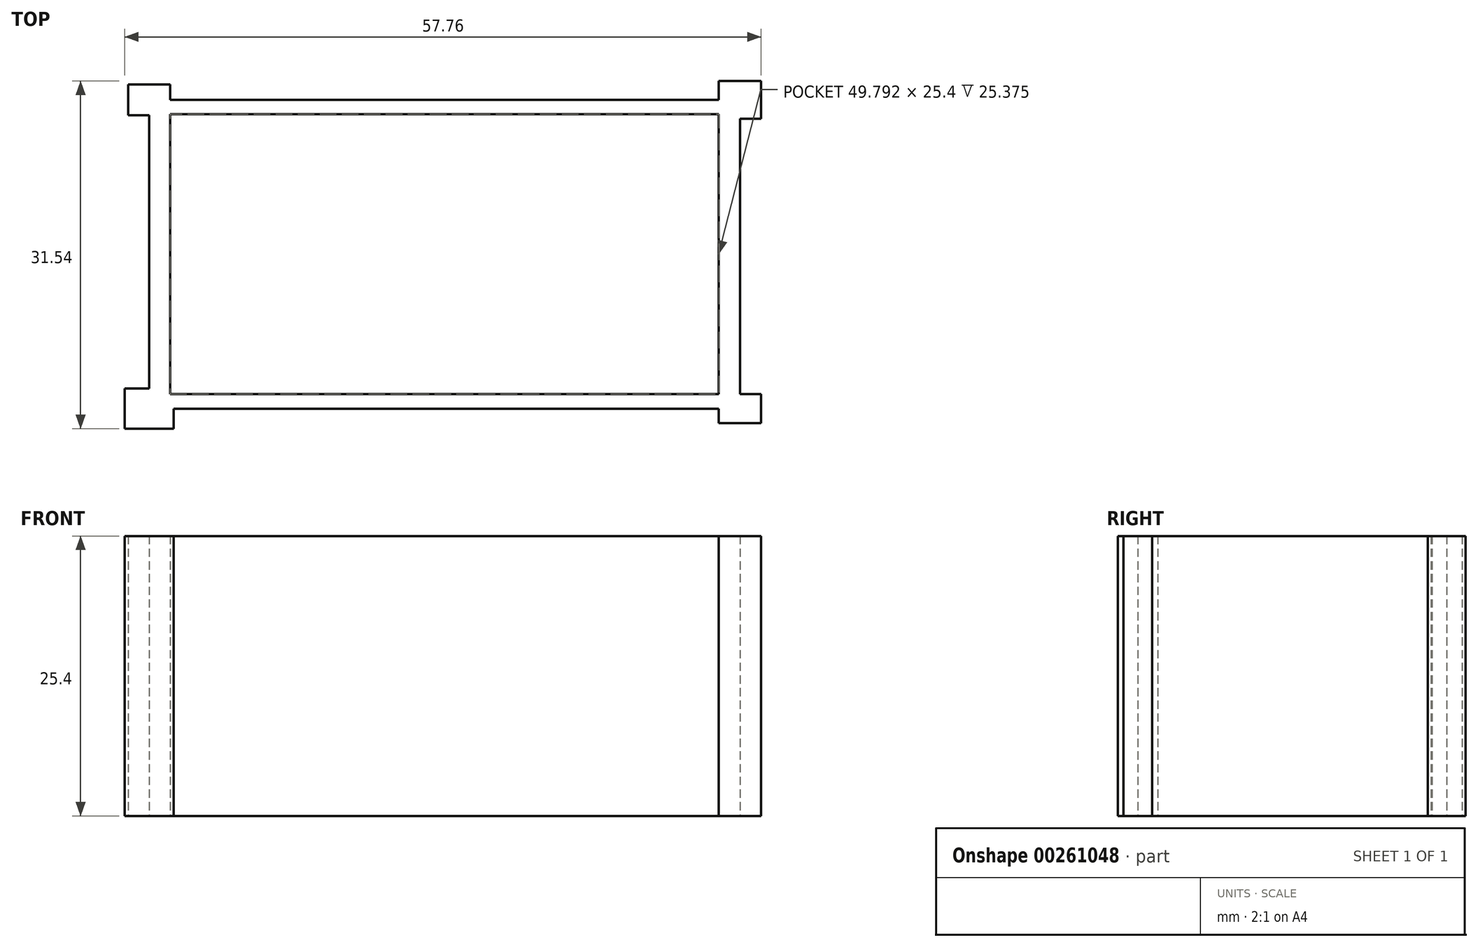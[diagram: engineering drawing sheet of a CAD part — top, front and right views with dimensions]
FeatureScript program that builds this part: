
annotation { "Feature Type Name" : "Feature", "Feature Type Description" : "" }
export const myFeature = defineFeature(function(context is Context, id is Id, definition is map)
    precondition{}
    {
        {
            var Q0;
            Q0=qCreatedBy(makeId("Top.planeOp"),FACE);
            var sketch = newSketch(context, id + "F0", { "sketchPlane" : qUnion([Q0])});
            skLineSegment(sketch, "E0.bottom", {"start": v(24.9, 14.01) * mm, "end": v(-24.9, 14.01) * mm});
            skLineSegment(sketch, "E0.top", {"start": v(24.9, -14.01) * mm, "end": v(-24.6, -14.01) * mm});
            skLineSegment(sketch, "E0.left", {"start": v(26.81, 12.3) * mm, "end": v(26.81, -12.7) * mm});
            skLineSegment(sketch, "E0.right", {"start": v(-26.81, 12.6) * mm, "end": v(-26.81, -12.2) * mm});
            skPoint(sketch, "E0.middle", {"position": v(0, 0) * mm});
            skLineSegment(sketch, "E1.bottom", {"start": v(24.9, 12.7) * mm, "end": v(-24.9, 12.7) * mm});
            skLineSegment(sketch, "E1.top", {"start": v(24.9, -12.7) * mm, "end": v(-24.9, -12.7) * mm});
            skLineSegment(sketch, "E1.left", {"start": v(24.9, 12.7) * mm, "end": v(24.9, -12.7) * mm});
            skLineSegment(sketch, "E1.right", {"start": v(-24.9, 12.7) * mm, "end": v(-24.9, -12.7) * mm});
            skLineSegment(sketch, "E2.bottom", {"start": v(24.9, 15.72) * mm, "end": v(28.73, 15.72) * mm});
            skLineSegment(sketch, "E2.top", {"start": v(26.81, 12.3) * mm, "end": v(28.73, 12.3) * mm});
            skLineSegment(sketch, "E2.left", {"start": v(24.9, 15.72) * mm, "end": v(24.9, 14.01) * mm});
            skLineSegment(sketch, "E2.right", {"start": v(28.73, 15.72) * mm, "end": v(28.73, 12.3) * mm});
            skPoint(sketch, "E2.middle", {"position": v(26.81, 14.01) * mm});
            skLineSegment(sketch, "E3.MirrorCS", {"start": v(28.73, 12.3) * mm, "end": v(26.81, 12.3) * mm});
            skLineSegment(sketch, "E4.MirrorCS", {"start": v(28.73, 15.72) * mm, "end": v(24.9, 15.72) * mm});
            skLineSegment(sketch, "E5.bottom", {"start": v(24.9, -15.32) * mm, "end": v(28.73, -15.32) * mm});
            skLineSegment(sketch, "E5.top", {"start": v(26.81, -12.7) * mm, "end": v(28.73, -12.7) * mm});
            skLineSegment(sketch, "E5.left", {"start": v(24.9, -15.32) * mm, "end": v(24.9, -14.01) * mm});
            skLineSegment(sketch, "E5.right", {"start": v(28.73, -15.32) * mm, "end": v(28.73, -12.7) * mm});
            skPoint(sketch, "E5.middle", {"position": v(26.81, -14.01) * mm});
            skLineSegment(sketch, "E6.bottom", {"start": v(-29.03, -15.82) * mm, "end": v(-24.6, -15.82) * mm});
            skLineSegment(sketch, "E6.top", {"start": v(-29.03, -12.2) * mm, "end": v(-26.81, -12.2) * mm});
            skLineSegment(sketch, "E6.left", {"start": v(-29.03, -15.82) * mm, "end": v(-29.03, -12.2) * mm});
            skLineSegment(sketch, "E6.right", {"start": v(-24.6, -15.82) * mm, "end": v(-24.6, -14.01) * mm});
            skPoint(sketch, "E6.middle", {"position": v(-26.81, -14.01) * mm});
            skLineSegment(sketch, "E7.bottom", {"start": v(-28.73, 12.6) * mm, "end": v(-26.81, 12.6) * mm});
            skLineSegment(sketch, "E7.top", {"start": v(-28.73, 15.42) * mm, "end": v(-24.9, 15.42) * mm});
            skLineSegment(sketch, "E7.left", {"start": v(-28.73, 12.6) * mm, "end": v(-28.73, 15.42) * mm});
            skLineSegment(sketch, "E7.right", {"start": v(-24.9, 12.6) * mm, "end": v(-24.9, 12.7) * mm});
            skPoint(sketch, "E7.middle", {"position": v(-26.81, 14.01) * mm});
            skPoint(sketch, "E8.orphan", {"position": v(24.9, -12.7) * mm});
            skPoint(sketch, "E9.orphan", {"position": v(24.9, 12.3) * mm});
            skLineSegment(sketch, "E10.trimOffspring", {"start": v(24.9, 12.7) * mm, "end": v(24.9, 12.3) * mm});
            skLineSegment(sketch, "E11.trimOffspring", {"start": v(-24.9, 14.01) * mm, "end": v(-24.9, 15.42) * mm});
            skLineSegment(sketch, "E12.trimOffspring", {"start": v(-24.9, -12.2) * mm, "end": v(-24.6, -12.2) * mm});
            skLineSegment(sketch, "E13.trimOffspring", {"start": v(-24.6, -12.7) * mm, "end": v(-24.6, -12.2) * mm});
            skPoint(sketch, "E14.MirrorCS.start.orphan", {"position": v(26.81, 12.3) * mm});
            skSolve(sketch);
        }
        {
            var Q0;
            Q0=makeQuery(id+"F0.imprint","IMPRINT",FACE,{"disambiguationData":[TD([[makeQuery(id+"F0.imprint","IMPRINT",EDGE,{"derivedFrom":sQuery(id+"F0.wireOp",EDGE,"E0.bottom")}),1.0]])]});
            extrude(context, id + "F1", {"entities" : qUnion([Q0]), "depth" : 25.4 * mm});
        }
        {
            var Q0;
            Q0=makeQuery(id+"F1.opExtrude","CAP_FACE",FACE,{"disambiguationData":[OSD([sQuery(id+"F0.wireOp",EDGE,"E0.bottom"),sQuery(id+"F0.wireOp",EDGE,"E0.top"),sQuery(id+"F0.wireOp",EDGE,"E0.left"),sQuery(id+"F0.wireOp",EDGE,"E0.right"),sQuery(id+"F0.wireOp",EDGE,"E1.bottom"),sQuery(id+"F0.wireOp",EDGE,"E1.top"),sQuery(id+"F0.wireOp",EDGE,"E1.left"),sQuery(id+"F0.wireOp",EDGE,"E1.right")])],"isStart":true});
            var sketch = newSketch(context, id + "F2", { "sketchPlane" : qUnion([Q0])});
            skLineSegment(sketch, "E15.bottom", {"start": v(24.9, 12.7) * mm, "end": v(-24.9, 12.7) * mm});
            skLineSegment(sketch, "E15.top", {"start": v(24.9, -12.7) * mm, "end": v(-24.9, -12.7) * mm});
            skLineSegment(sketch, "E15.left", {"start": v(24.9, 12.7) * mm, "end": v(24.9, -12.7) * mm});
            skLineSegment(sketch, "E15.right", {"start": v(-24.9, 12.7) * mm, "end": v(-24.9, -12.7) * mm});
            skPoint(sketch, "E15.middle", {"position": v(0, 0) * mm});
            skSolve(sketch);
        }
        {
            var Q0;
            Q0 = qSketchRegion(id + "F2", true);
            extrude(context, id + "F3", {"entities" : qUnion([Q0]), "operationType" : NewBodyOperationType.ADD, "oppositeDirection" : true, "depth" : 0.03 * mm});
        }
    });
